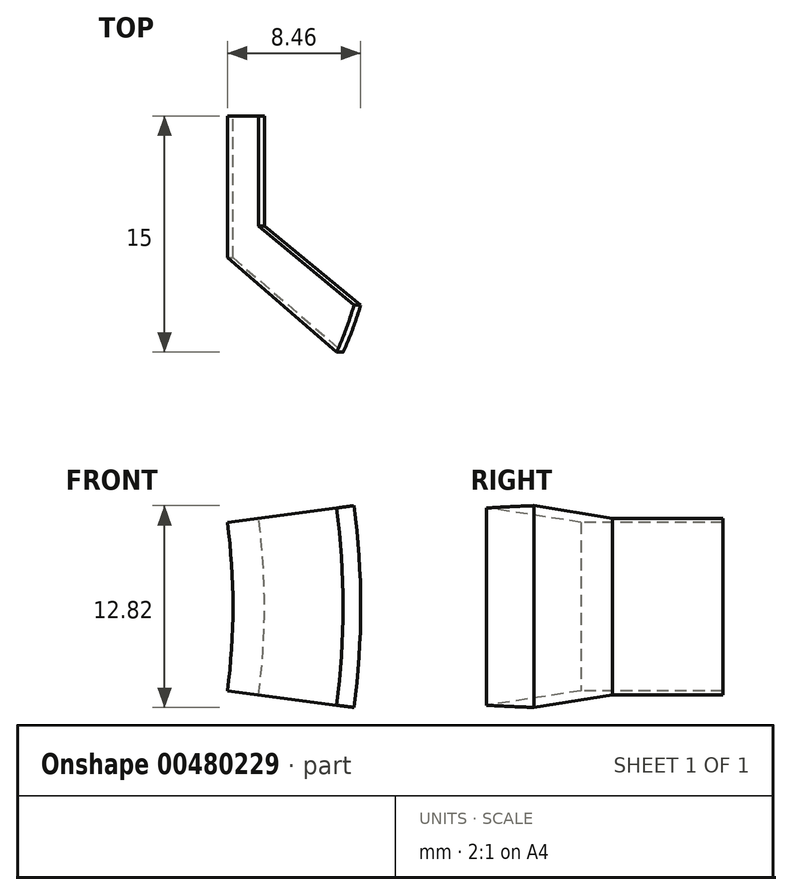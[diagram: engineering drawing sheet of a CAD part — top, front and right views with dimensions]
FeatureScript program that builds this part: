
annotation { "Feature Type Name" : "Feature", "Feature Type Description" : "" }
export const myFeature = defineFeature(function(context is Context, id is Id, definition is map)
    precondition{}
    {
        {
            var Q0;
            Q0=qCreatedBy(makeId("Top.planeOp"),FACE);
            var sketch = newSketch(context, id + "F0", { "sketchPlane" : qUnion([Q0])});
            skEllipse(sketch, "E0", {"center": v(0, 0) * mm, "majorRadius": 50 * mm, "minorRadius": 32.5 * mm, "majorAxis": v(1, 0)});
            skLineSegment(sketch, "E1", {"start": v(49.1, -6.13) * mm, "end": v(42.99, -1.13) * mm});
            skLineSegment(sketch, "E2", {"start": v(42.99, -1.13) * mm, "end": v(42.99, 5.87) * mm});
            skLineSegment(sketch, "E3", {"start": v(42.99, 5.87) * mm, "end": v(40.99, 5.87) * mm});
            skLineSegment(sketch, "E4", {"start": v(40.99, 5.87) * mm, "end": v(40.99, -3.13) * mm});
            skLineSegment(sketch, "E5", {"start": v(40.99, -3.13) * mm, "end": v(47.99, -9.13) * mm});
            skLineSegment(sketch, "E6", {"start": v(0, 50.65) * mm, "end": v(0, -40.65) * mm, "construction": true});
            skPoint(sketch, "E6.endSnap0", {"position": v(0, -32.5) * mm});
            skLineSegment(sketch, "E7", {"start": v(0, 32.5) * mm, "end": v(50, 0) * mm, "construction": true});
            skSolve(sketch);
        }
        {
            var Q0;
            {var subQ0=sQuery(id+"F0.wireOp",EDGE,"E1");Q0=makeQuery(id+"F0.imprint","IMPRINT",FACE,{"disambiguationData":[TD([[makeQuery(id+"F0.imprint","IMPRINT",EDGE,{"derivedFrom":subQ0}),1.0]])]});}
            var Q1;
            Q1=sQuery(id+"F0.wireOp",EDGE,"E6");
            revolve(context, id + "F1", {"entities" : qUnion([Q0]), "axis" : qUnion([Q1]), "revolveType" : RevolveType.SYMMETRIC, "angle" : 15 * degree});
        }
    });
